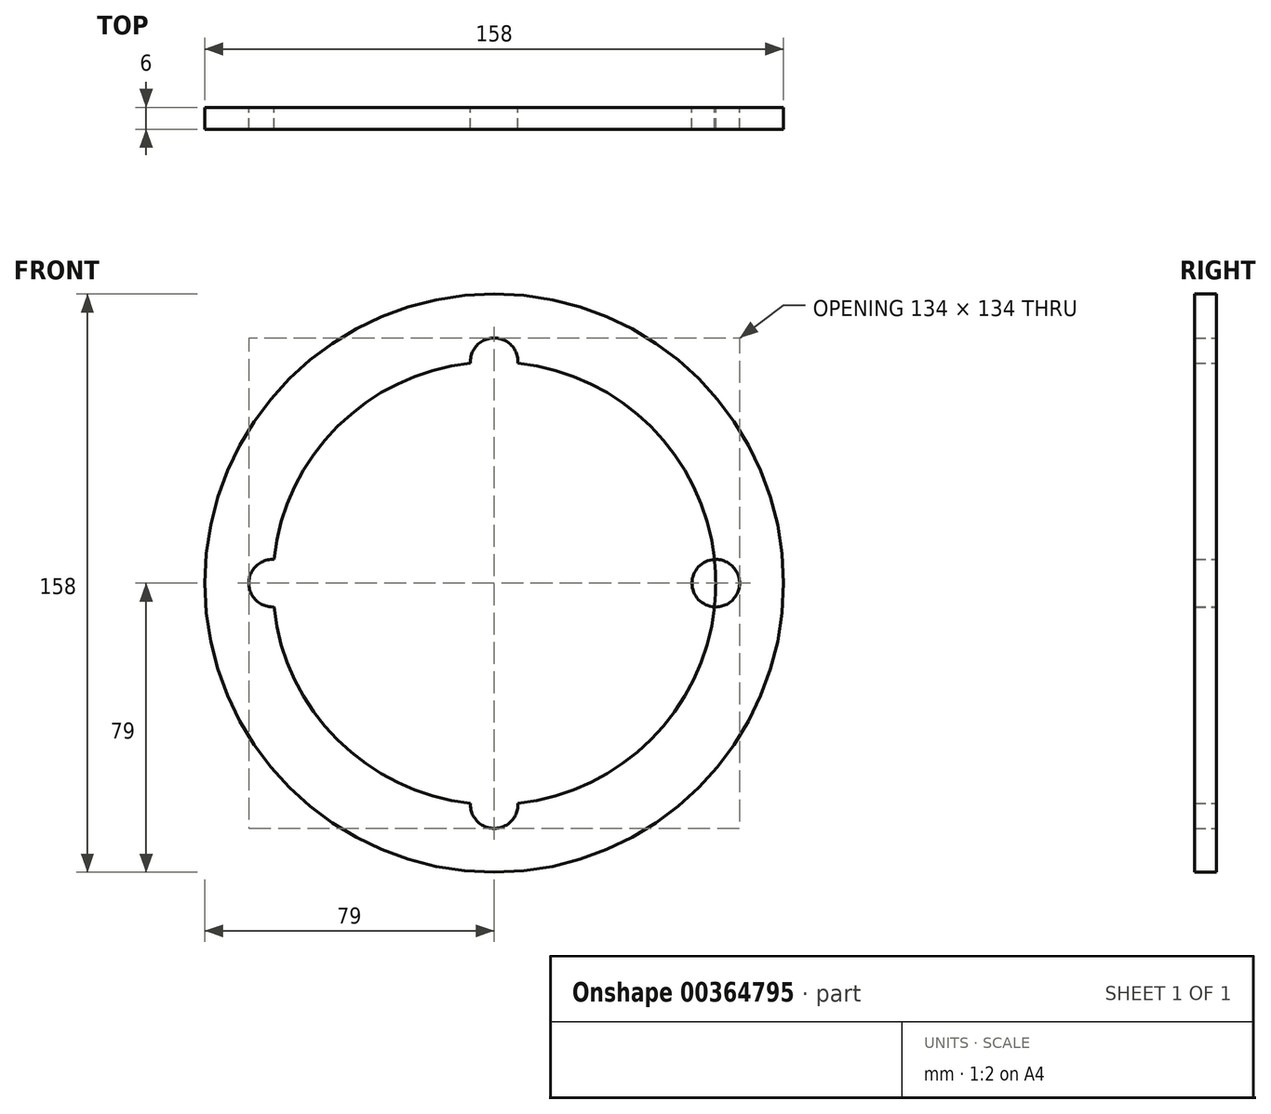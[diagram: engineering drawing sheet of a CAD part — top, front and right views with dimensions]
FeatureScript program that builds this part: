
annotation { "Feature Type Name" : "Feature", "Feature Type Description" : "" }
export const myFeature = defineFeature(function(context is Context, id is Id, definition is map)
    precondition{}
    {
        {
            var Q0;
            Q0=qCreatedBy(makeId("Front.planeOp"),FACE);
            var sketch = newSketch(context, id + "F0", { "sketchPlane" : qUnion([Q0])});
            skCircle(sketch, "E0", {"center": v(0, 0) * mm, "radius": 79 * mm});
            skCircle(sketch, "E1", {"center": v(0, 0) * mm, "radius": 60.5 * mm});
            skLineSegment(sketch, "E2", {"start": v(0, 0) * mm, "end": v(0, 60.5) * mm});
            skCircle(sketch, "E3", {"center": v(0, 60.5) * mm, "radius": 6.5 * mm});
            skCircle(sketch, "E4.1.0", {"center": v(-60.5, 0) * mm, "radius": 6.5 * mm});
            skCircle(sketch, "E4.2.0", {"center": v(0, -60.5) * mm, "radius": 6.5 * mm});
            skCircle(sketch, "E4.3.0", {"center": v(60.5, 0) * mm, "radius": 6.5 * mm});
            skSolve(sketch);
        }
        {
            var Q0;
            Q0=makeQuery(id+"F0.imprint","IMPRINT",FACE,{"disambiguationData":[TD([[makeQuery(id+"F0.imprint","IMPRINT",EDGE,{"derivedFrom":sQuery(id+"F0.wireOp",EDGE,"E0")}),1.0]])]});
            var Q1;
            {var subQ1=sQuery(id+"F0.wireOp",EDGE,"E1");var subQ8=sQuery(id+"F0.wireOp",EDGE,"E4.3.0");var subQ12=makeQuery(id+"F0.imprint","INTERSECT",VERTEX,{"disambiguationData":[OD(0.0)],"derivedFrom":[subQ1,subQ8]});Q1=makeQuery(id+"F0.imprint","IMPRINT",FACE,{"disambiguationData":[TD([[makeQuery(id+"F0.imprint","IMPRINT",EDGE,{"disambiguationData":[TD([[subQ12,1.0]])],"derivedFrom":subQ1}),1.0]])]});}
            extrude(context, id + "F1", {"entities" : qUnion([Q0, Q1]), "depth" : 6 * mm, "offsetDistance" : 25 * mm});
        }
        {
            var Q0;
            Q0=makeQuery(id+"F1.opExtrude","CAP_FACE",FACE,{"disambiguationData":[OSD([sQuery(id+"F0.wireOp",EDGE,"E0"),sQuery(id+"F0.wireOp",EDGE,"E3"),sQuery(id+"F0.wireOp",EDGE,"E4.1.0"),sQuery(id+"F0.wireOp",EDGE,"E4.2.0"),sQuery(id+"F0.wireOp",EDGE,"E4.3.0")])],"isStart":true});
            var sketch = newSketch(context, id + "F2", { "sketchPlane" : qUnion([Q0])});
            skCircle(sketch, "E5", {"center": v(0, 0) * mm, "radius": 39.5 * mm});
            skSolve(sketch);
        }
        {
            var Q0;
            Q0=makeQuery(id+"F2.imprint","IMPRINT",FACE,{"disambiguationData":[TD([[makeQuery(id+"F2.imprint","IMPRINT",EDGE,{"derivedFrom":sQuery(id+"F2.wireOp",EDGE,"E5")}),1.0]])]});
            extrude(context, id + "F3", {"entities" : qUnion([Q0]), "operationType" : NewBodyOperationType.REMOVE, "endBound" : BoundingType.THROUGH_ALL, "oppositeDirection" : true, "depth" : 25 * mm, "offsetDistance" : 25 * mm});
        }
    });
